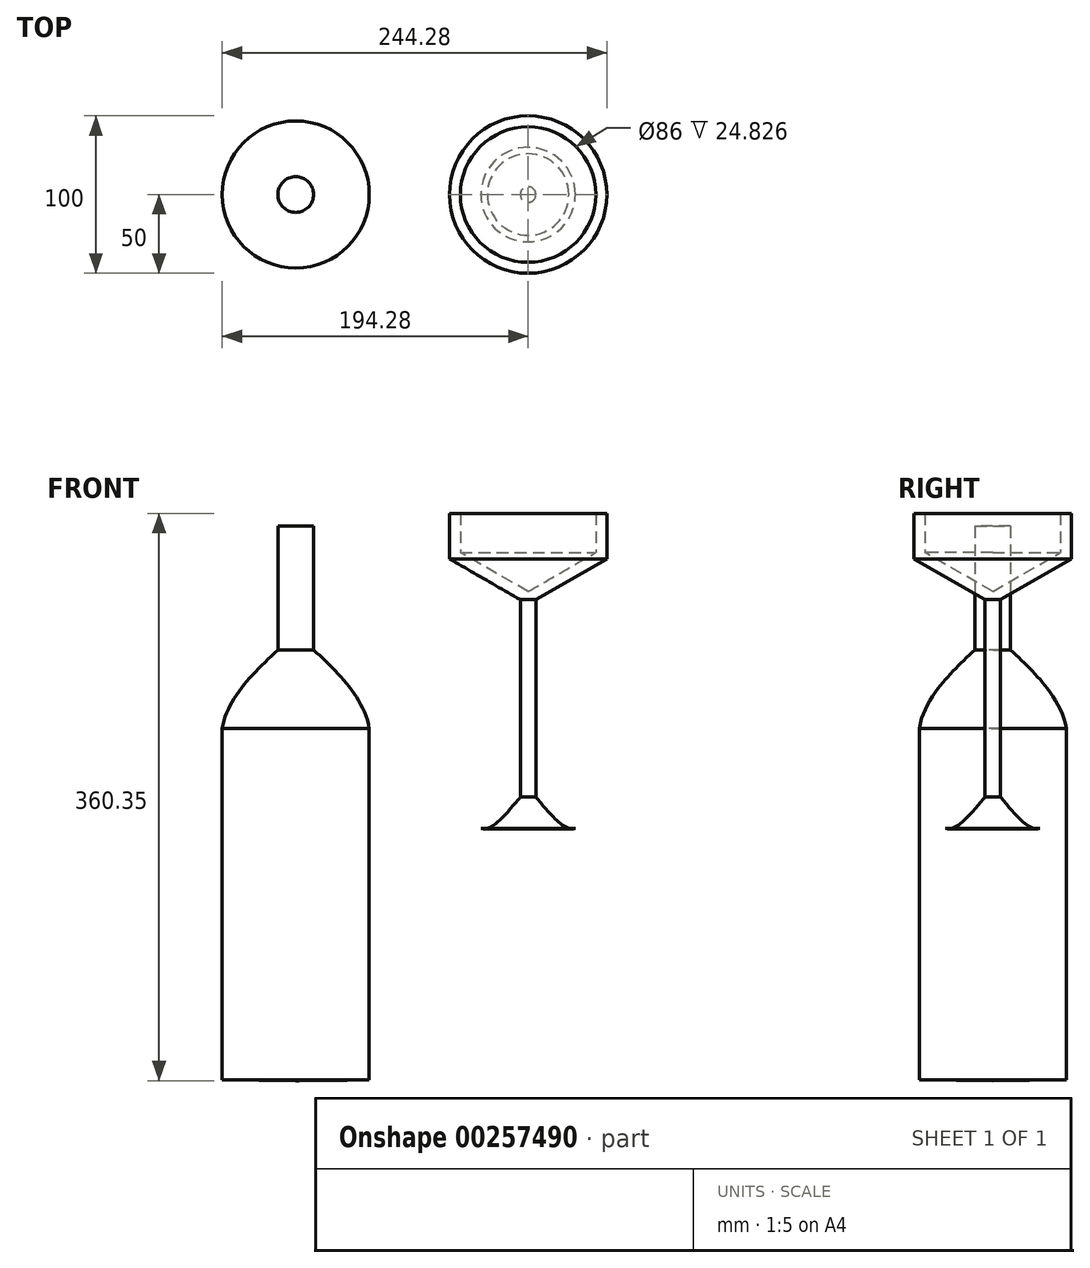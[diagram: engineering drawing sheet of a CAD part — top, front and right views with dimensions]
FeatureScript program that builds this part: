
annotation { "Feature Type Name" : "Feature", "Feature Type Description" : "" }
export const myFeature = defineFeature(function(context is Context, id is Id, definition is map)
    precondition{}
    {
        {
            var Q0;
            Q0=qCreatedBy(makeId("Front.planeOp"),FACE);
            var sketch = newSketch(context, id + "F0", { "sketchPlane" : qUnion([Q0])});
            skLineSegment(sketch, "E0", {"start": v(0, 0) * mm, "end": v(0, 150.35) * mm});
            skLineSegment(sketch, "E1", {"start": v(43, 200) * mm, "end": v(50, 200) * mm});
            skLineSegment(sketch, "E2", {"start": v(0, 0) * mm, "end": v(30, 0) * mm});
            skPoint(sketch, "E3.end.orphan", {"position": v(0, 118.26) * mm});
            skPoint(sketch, "E3.start.orphan", {"position": v(81.74, 200) * mm});
            skLineSegment(sketch, "E4", {"start": v(4.96, 7.7) * mm, "end": v(4.96, 150.37) * mm});
            skArc(sketch, "E5.cCircle", {"start": v(0, 150) * mm, "mid": v(2.48, 150.06) * mm, "end": v(4.96, 150.25) * mm, "construction": true});
            skLineSegment(sketch, "E5.0", {"start": v(50, 200) * mm, "end": v(50, 171.13) * mm});
            skLineSegment(sketch, "E5.1", {"start": v(50, 171.13) * mm, "end": v(0, 142.26) * mm});
            skPoint(sketch, "E5.0.midPoint", {"position": v(50, 200) * mm});
            skPoint(sketch, "E6.orphan", {"position": v(50, 228.87) * mm});
            skLineSegment(sketch, "E7.0", {"start": v(43, 175.17) * mm, "end": v(-3.5, 148.33) * mm});
            skLineSegment(sketch, "E7.1", {"start": v(43, 200) * mm, "end": v(43, 175.17) * mm});
            skLineSegment(sketch, "E8.0", {"start": v(43, 195) * mm, "end": v(50, 195) * mm});
            skPoint(sketch, "E9", {"position": v(15, 0) * mm});
            skPoint(sketch, "E10.1.internal.orphan", {"position": v(15, 10.84) * mm});
            skPoint(sketch, "E10.2.internal.orphan", {"position": v(4.96, 19.86) * mm});
            skFitSpline(sketch, "E11", {"points": [v(4.96, 19.86) * mm, v(30, 0) * mm, v(52.2, 59.68) * mm, v(84.06, 135.6) * mm], "startDerivative": vector(109.75, -134.29) * mm, "endDerivative": vector(87.55, 174.88) * mm});
            skSolve(sketch);
        }
        {
            var Q0;
            Q0 = qSketchRegion(id + "F0", true);
            var Q1;
            Q1=sQuery(id+"F0.wireOp",EDGE,"E0");
            revolve(context, id + "F1", {"entities" : qUnion([Q0]), "axis" : qUnion([Q1]), "revolveType" : RevolveType.FULL});
        }
        {
            var Q0;
            Q0=qCreatedBy(makeId("Front.planeOp"),FACE);
            var sketch = newSketch(context, id + "F2", { "sketchPlane" : qUnion([Q0])});
            skLineSegment(sketch, "E12", {"start": v(-147.57, -160.35) * mm, "end": v(-147.57, 191.83) * mm});
            skLineSegment(sketch, "E13", {"start": v(-147.57, 191.83) * mm, "end": v(-136.22, 191.83) * mm});
            skLineSegment(sketch, "E14", {"start": v(-136.22, 191.83) * mm, "end": v(-136.22, 113.3) * mm});
            skLineSegment(sketch, "E15", {"start": v(-100.86, 63.41) * mm, "end": v(-100.86, -159.85) * mm});
            skLineSegment(sketch, "E16", {"start": v(-100.86, -159.85) * mm, "end": v(-147.57, -160.35) * mm});
            skFitSpline(sketch, "E17", {"points": [v(-136.22, 113.3) * mm, v(-100.86, 63.41) * mm, v(-123.85, -20.15) * mm], "startDerivative": vector(104.8, -99.12) * mm, "endDerivative": vector(-74.86, -165.84) * mm});
            skSolve(sketch);
        }
        {
            var Q0;
            Q0=makeQuery(id+"F2.imprint","IMPRINT",FACE,{"disambiguationData":[TD([[makeQuery(id+"F2.imprint","IMPRINT",EDGE,{"derivedFrom":sQuery(id+"F2.wireOp",EDGE,"E12")}),-1.0]])]});
            var Q1;
            Q1=sQuery(id+"F2.wireOp",EDGE,"E12");
            revolve(context, id + "F3", {"entities" : qUnion([Q0]), "axis" : qUnion([Q1]), "revolveType" : RevolveType.FULL});
        }
    });
